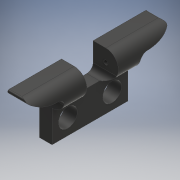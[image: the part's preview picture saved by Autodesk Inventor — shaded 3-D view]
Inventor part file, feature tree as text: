
AUTODESK INVENTOR PART (.ipt)
format: ipt  version: 2018 (Build 220112000, 112)  size: 218,112 bytes
history: native  units: mm
features: sketch x5, extrude x4, projected_geometry x4, hole x1, mirror x1
ambient origin geometry x8: Origin, YZ Plane, XZ Plane, XY Plane, X Axis, Y Axis, Z Axis, Center Point
bodies: Solid1 (feature_tree)
feature tree (15):
  extrude  "Extrusion1"  Depth=2.0mm
  hole  "Hole1"  [1 undecoded]
  extrude  "Extrusion2"  Depth=1.0mm
  extrude  "Extrusion3"  Depth=10.0mm TaperAngle=0.0deg
  extrude  "Extrusion4"  Depth=10.0mm TaperAngle=0.0deg
  mirror  "Mirror1"
  sketch  "Sketch1"  dims[d0=5.0mm d1=2.0mm]
  sketch  "Sketch2"  dims[d2=2.0mm d3=0.7mm]
  projected_geometry  "Projected Loop1"
  sketch  "Sketch3"  dims[d4=12.0mm d5=0.0mm]
  projected_geometry  "Projected Loop2"
  sketch  "Sketch4"  dims[d6=3.0mm d7=6.0mm d8=3.023mm d9=2.0mm d10=14.3117mm d11=8.0mm d12=20.594885mm d13=1.0mm]
  projected_geometry  "Projected Loop3"
  sketch  "Sketch5"  dims[d14=5.0mm d15=10.0mm d16=0.0mm d17=10.0mm d18=0.0mm d19=7.0mm d20=10.0mm d21=0.0mm d22=0.25mm d23=5.923523mm]
  projected_geometry  "Projected Loop4"
note: 1 required parameter value undecoded (feature->parameter linkage not recoverable at this tier; creation-order binding heuristic only, values carry confidence <= 0.55)
